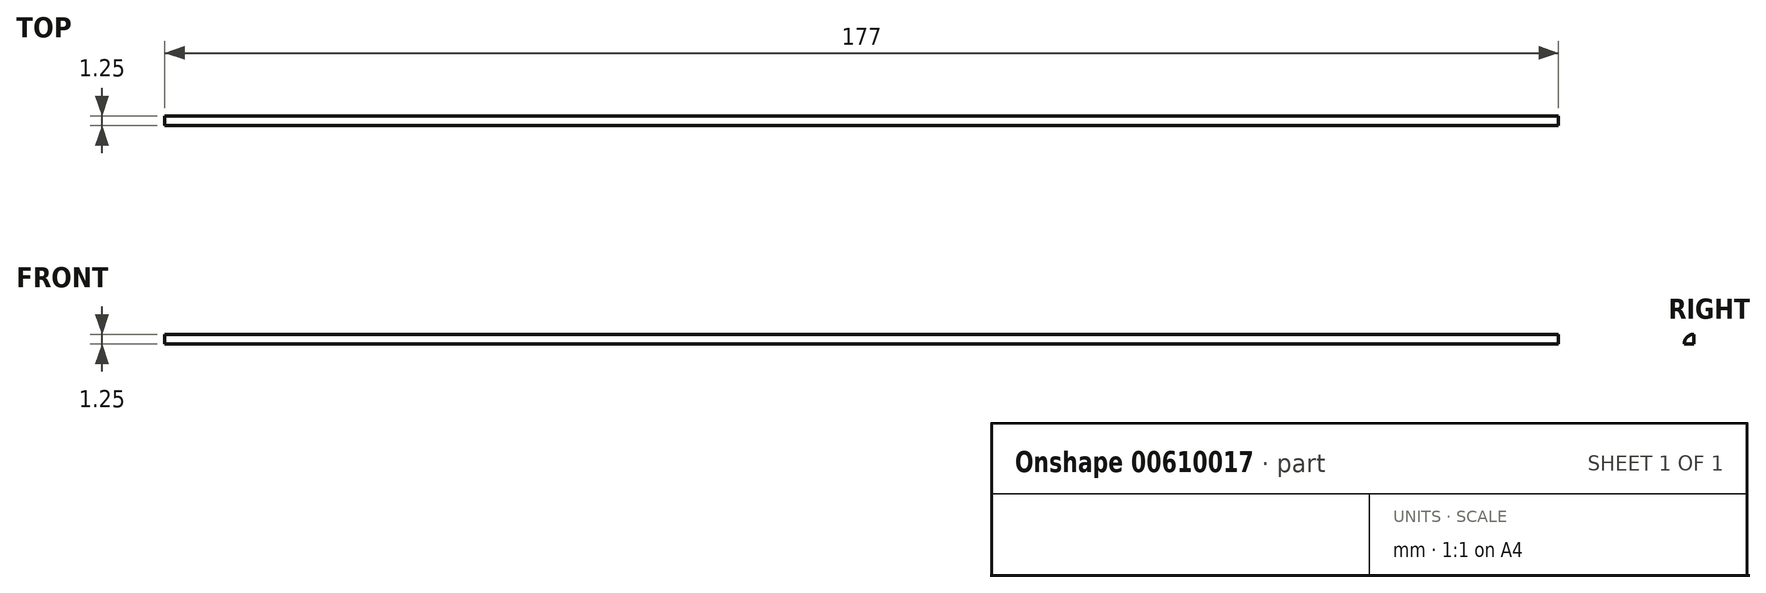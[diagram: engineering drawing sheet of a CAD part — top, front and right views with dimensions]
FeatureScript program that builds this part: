
annotation { "Feature Type Name" : "Feature", "Feature Type Description" : "" }
export const myFeature = defineFeature(function(context is Context, id is Id, definition is map)
    precondition{}
    {
        {
            var Q0;
            Q0=qCreatedBy(makeId("Right.planeOp"),FACE);
            var sketch = newSketch(context, id + "F0", { "sketchPlane" : qUnion([Q0])});
            skArc(sketch, "E0", {"start": v(0, 1.25) * mm, "mid": v(-0.88, 0.88) * mm, "end": v(-1.25, 0) * mm});
            skLineSegment(sketch, "E1.bottom", {"start": v(-1.25, 0) * mm, "end": v(0, 0) * mm});
            skLineSegment(sketch, "E2.bottom", {"start": v(1.27, 0) * mm, "end": v(1.37, 0) * mm});
            skLineSegment(sketch, "E2.left", {"start": v(0, 0) * mm, "end": v(0, 1.25) * mm});
            skLineSegment(sketch, "E3.trimOffspring", {"start": v(1.25, 0) * mm, "end": v(1.27, 0) * mm});
            skSolve(sketch);
        }
        {
            var Q0;
            Q0 = qSketchRegion(id + "F0", true);
            extrude(context, id + "F1", {"entities" : qUnion([Q0]), "depth" : 177 * mm, "offsetDistance" : 25 * mm});
        }
    });
